# Revit family: Haworth_Accessory_MonitorArm_HeavyDutySingleStraight
name_source: partatom
category: Furniture Systems
revit_build: Autodesk Revit 2018 (Build: 20170223_1515(x64)
units: mm (PartAtom-declared; Revit-internal decimal feet)

## family parameters
Always vertical = Yes
Cut with Voids When Loaded = No
OmniClass Number = 23.40.70.14.64.21
OmniClass Title = Systems Furniture
Part Type = Normal
Room Calculation Point = No
Round Connector Dimension = Use Diameter
Shared = No
Work Plane-Based = No

## types (1)
- Single Monitor Arm
    Actual Depth = 1 1/4"
    Assembly Code = E2020200
    Base of Arm = 0"
    Description = Haworth - Accessory - Monitor Arm - Heavy Duty - Single - Straight
    Manufacturer = Haworth
    Model = Haworth - Accessory - Monitor Arm - Heavy Duty - Single - Straight
    Monitor Frame = 1/4"
    Monitor Frame Finish = Haworth - Monitor Frame
    Monitor Height = 14"
    Monitor Screen Finish = Haworth - Monitor Screen
    Monitor Width = 22"
    Post Base = 2 9/32"
    Revision Number = 3
    Single = Yes
    Single Monitor Location = 0"
    Size = Verify Final Dim. w/ Haworth
    Spacer = 0"
    Sustainability Info = http://www.haworth.com
    Tool Rail = 4 3/8"
    Tool Rail Mounting Height = 7 7/16"
    Trim Finish = Haworth _ Paint _ Metallic Champagne
    URL = www.haworth.com
    URL - Product = http://www.haworth.com
    Warranty = http://www.haworth.com

## geometry (parser evidence)
native form markers: Sweep x14
no freeform markers — native parametric forms only
